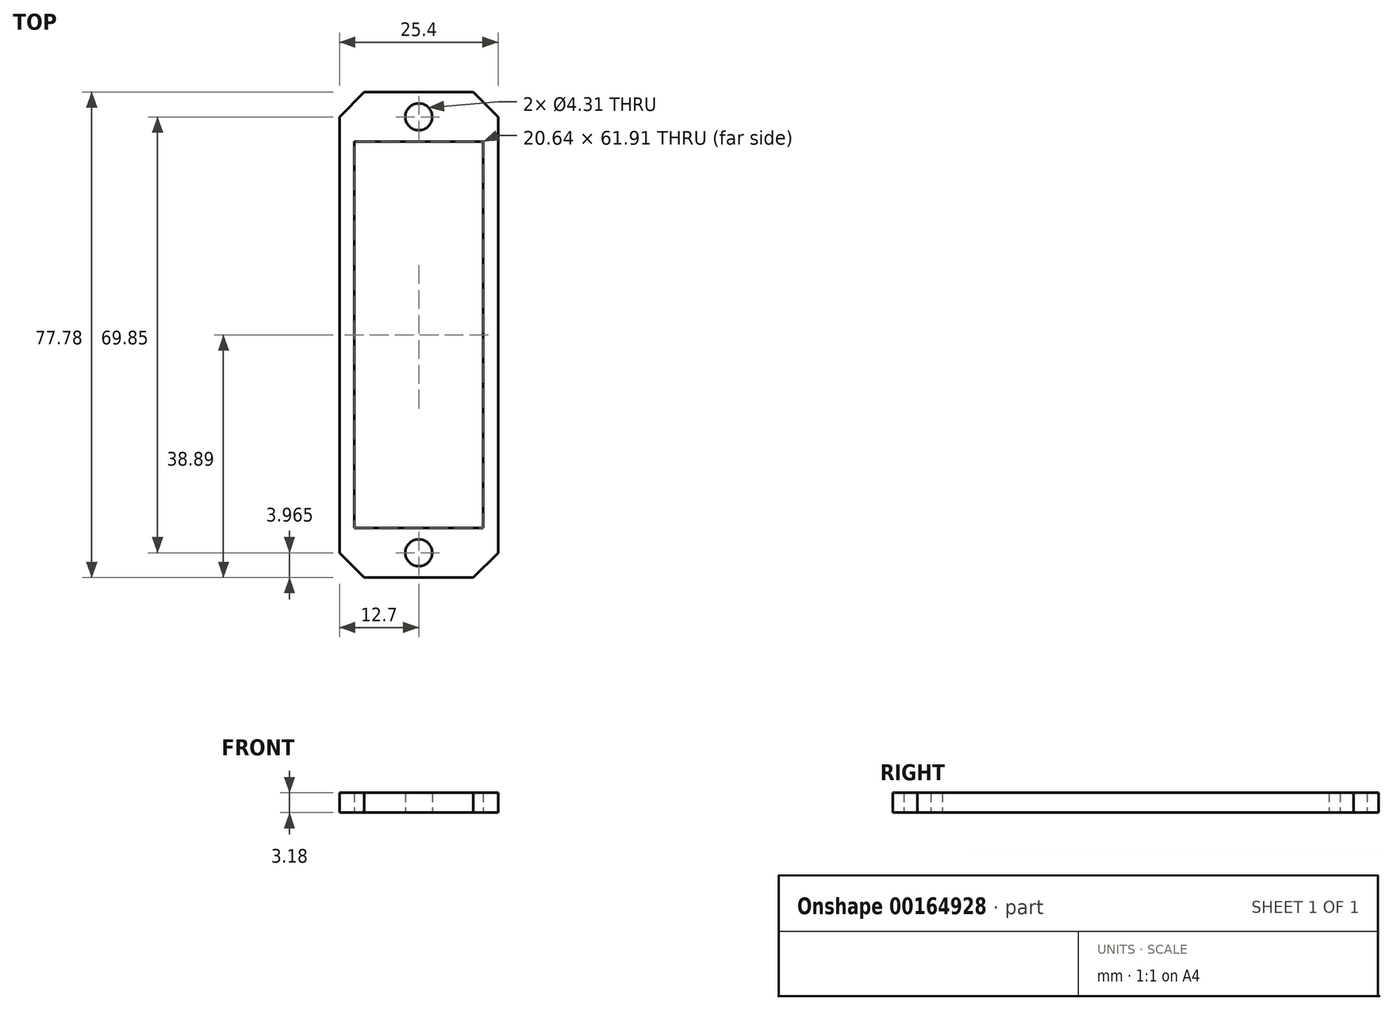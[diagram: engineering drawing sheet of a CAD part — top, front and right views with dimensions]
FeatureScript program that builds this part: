
annotation { "Feature Type Name" : "Feature", "Feature Type Description" : "" }
export const myFeature = defineFeature(function(context is Context, id is Id, definition is map)
    precondition{}
    {
        {
            var Q0;
            Q0=qCreatedBy(makeId("Top.planeOp"),FACE);
            var sketch = newSketch(context, id + "F0", { "sketchPlane" : qUnion([Q0])});
            skLineSegment(sketch, "E0.bottom", {"start": v(-10.32, 30.96) * mm, "end": v(10.32, 30.96) * mm});
            skLineSegment(sketch, "E0.top", {"start": v(-10.32, -30.96) * mm, "end": v(10.32, -30.96) * mm});
            skLineSegment(sketch, "E0.left", {"start": v(-10.32, 30.96) * mm, "end": v(-10.32, -30.96) * mm});
            skLineSegment(sketch, "E0.right", {"start": v(10.32, 30.96) * mm, "end": v(10.32, -30.96) * mm});
            skPoint(sketch, "E0.middle", {"position": v(0, 0) * mm});
            skLineSegment(sketch, "E1.bottom", {"start": v(-12.7, 38.9) * mm, "end": v(12.7, 38.9) * mm});
            skLineSegment(sketch, "E1.top", {"start": v(-12.7, -38.9) * mm, "end": v(12.7, -38.9) * mm});
            skLineSegment(sketch, "E1.left", {"start": v(-12.7, 38.9) * mm, "end": v(-12.7, -38.9) * mm});
            skLineSegment(sketch, "E1.right", {"start": v(12.7, 38.9) * mm, "end": v(12.7, -38.9) * mm});
            skLineSegment(sketch, "E2", {"start": v(0, 30.96) * mm, "end": v(0, 38.9) * mm, "construction": true});
            skLineSegment(sketch, "E3", {"start": v(0, -30.96) * mm, "end": v(0, -38.9) * mm, "construction": true});
            skLineSegment(sketch, "E4", {"start": v(10.32, 0) * mm, "end": v(12.7, 0) * mm, "construction": true});
            skCircle(sketch, "E5", {"center": v(0, 34.93) * mm, "radius": 2.15 * mm});
            skCircle(sketch, "E6", {"center": v(0, -34.93) * mm, "radius": 2.15 * mm});
            skSolve(sketch);
        }
        {
            var Q0;
            Q0=makeQuery(id+"F0.imprint","IMPRINT",FACE,{"disambiguationData":[TD([[makeQuery(id+"F0.imprint","IMPRINT",EDGE,{"derivedFrom":sQuery(id+"F0.wireOp",EDGE,"E0.bottom")}),1.0]])]});
            extrude(context, id + "F1", {"entities" : qUnion([Q0]), "depth" : 3.17 * mm});
        }
        {
            var Q0;
            Q0=makeQuery(id+"F1.opExtrude","SWEPT_EDGE",EDGE,{"disambiguationData":[OSD([sQuery(id+"F0.wireOp",EDGE,"E1.top"),sQuery(id+"F0.wireOp",EDGE,"E1.left")])]});
            var Q1;
            Q1=makeQuery(id+"F1.opExtrude","SWEPT_EDGE",EDGE,{"disambiguationData":[OSD([sQuery(id+"F0.wireOp",EDGE,"E1.top"),sQuery(id+"F0.wireOp",EDGE,"E1.right")])]});
            var Q2;
            Q2=makeQuery(id+"F1.opExtrude","SWEPT_EDGE",EDGE,{"disambiguationData":[OSD([sQuery(id+"F0.wireOp",EDGE,"E1.bottom"),sQuery(id+"F0.wireOp",EDGE,"E1.right")])]});
            var Q3;
            Q3=makeQuery(id+"F1.opExtrude","SWEPT_EDGE",EDGE,{"disambiguationData":[OSD([sQuery(id+"F0.wireOp",EDGE,"E1.bottom"),sQuery(id+"F0.wireOp",EDGE,"E1.left")])]});
            chamfer(context, id + "F2", {"entities" : qUnion([Q0, Q1, Q2, Q3]), "width" : 3.97 * mm, "tangentPropagation" : true});
        }
    });
